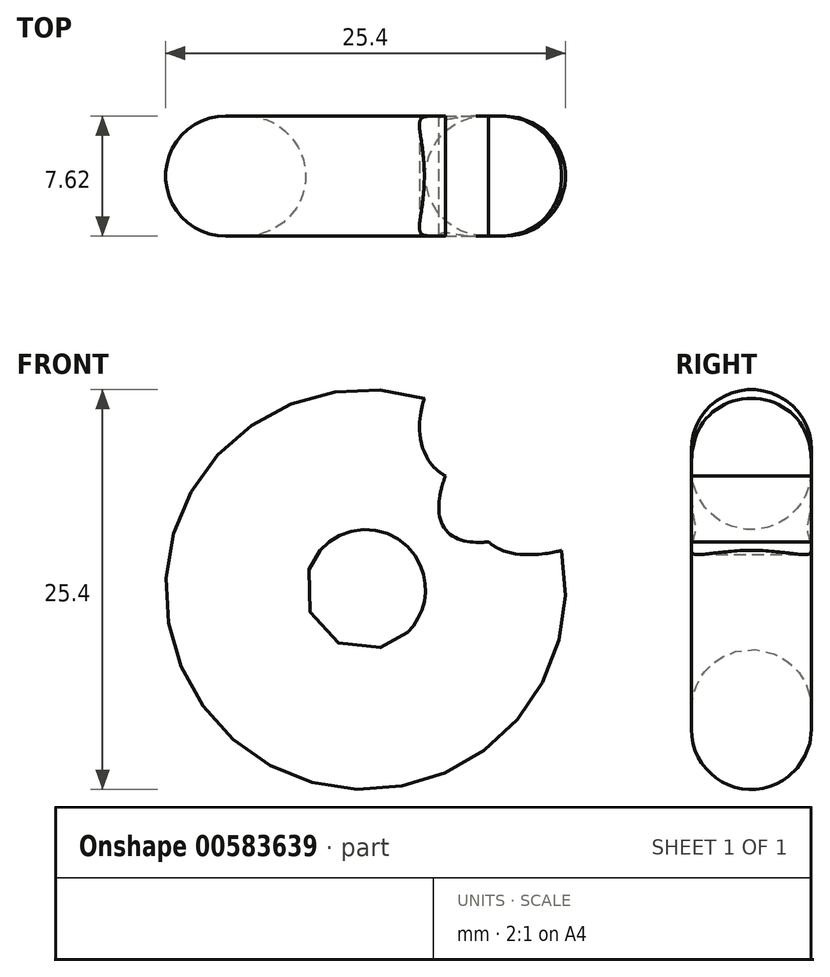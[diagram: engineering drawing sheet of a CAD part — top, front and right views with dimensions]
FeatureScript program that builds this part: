
annotation { "Feature Type Name" : "Feature", "Feature Type Description" : "" }
export const myFeature = defineFeature(function(context is Context, id is Id, definition is map)
    precondition{}
    {
        {
            var Q0;
            Q0=qCreatedBy(makeId("Front.planeOp"),FACE);
            var sketch = newSketch(context, id + "F0", { "sketchPlane" : qUnion([Q0])});
            skArc(sketch, "E0", {"start": v(0, 12.7) * mm, "mid": v(-8.98, -8.98) * mm, "end": v(12.7, 0) * mm});
            skArc(sketch, "E1", {"start": v(0, 3.81) * mm, "mid": v(-2.7, -2.7) * mm, "end": v(3.81, 0) * mm});
            skArc(sketch, "E2", {"start": v(0, 12.7) * mm, "mid": v(8.98, 8.98) * mm, "end": v(12.7, 0) * mm});
            skArc(sketch, "E3", {"start": v(0, 3.81) * mm, "mid": v(2.7, 2.7) * mm, "end": v(3.81, 0) * mm});
            skPoint(sketch, "E4", {"position": v(8.98, 8.98) * mm});
            skEllipse(sketch, "E5", {"center": v(8.98, 12.27) * mm, "majorRadius": 6.46 * mm, "minorRadius": 4.47 * mm, "majorAxis": v(-0.7, -0.7)});
            skEllipse(sketch, "E6", {"center": v(13.9, 7.03) * mm, "majorRadius": 7.35 * mm, "minorRadius": 3.72 * mm, "majorAxis": v(-0.88, -0.48)});
            skEllipticalArc(sketch, "E7", {});
            const initialGuessF0  = {"E7": [0.017075618728995323, 0.013890886679291725, -0.762498905092994, -0.6469895051173437, 0.015677614206353045, 0.0052293633850373335, 4.771161160451003, 1.5778972296702722]};
            skSetInitialGuess(sketch, initialGuessF0);
            skSolve(sketch);
        }
        {
            var Q0;
            Q0=makeQuery(id+"F0.imprint","IMPRINT",FACE,{"disambiguationData":[TD([[makeQuery(id+"F0.imprint","IMPRINT",EDGE,{"derivedFrom":sQuery(id+"F0.wireOp",EDGE,"E0")}),1.0]])]});
            extrude(context, id + "F1", {"entities" : qUnion([Q0]), "depth" : 7.62 * mm, "offsetDistance" : 25.4 * mm});
        }
        {
            var Q0;
            Q0=makeQuery(id+"F1.opExtrude","CAP_EDGE",EDGE,{"disambiguationData":[OSD([sQuery(id+"F0.wireOp",EDGE,"E0"),sQuery(id+"F0.wireOp",EDGE,"E2")])],"isStart":true});
            var Q1;
            Q1=makeQuery(id+"F1.opExtrude","CAP_EDGE",EDGE,{"disambiguationData":[OSD([sQuery(id+"F0.wireOp",EDGE,"E0"),sQuery(id+"F0.wireOp",EDGE,"E2")])],"isStart":false});
            fillet(context, id + "F2", {"entities" : qUnion([Q0, Q1]), "radius" : 3.8 * mm, "tangentPropagation" : true, "allowEdgeOverflow" : false});
        }
        {
            var Q0;
            Q0=makeQuery(id+"F1.opExtrude","CAP_EDGE",EDGE,{"disambiguationData":[OSD([sQuery(id+"F0.wireOp",EDGE,"E1"),sQuery(id+"F0.wireOp",EDGE,"E3")])],"isStart":true});
            var Q1;
            Q1=makeQuery(id+"F1.opExtrude","CAP_EDGE",EDGE,{"disambiguationData":[OSD([sQuery(id+"F0.wireOp",EDGE,"E1"),sQuery(id+"F0.wireOp",EDGE,"E3")])],"isStart":false});
            fillet(context, id + "F3", {"entities" : qUnion([Q0, Q1]), "radius" : 3.8 * mm, "tangentPropagation" : true, "allowEdgeOverflow" : false});
        }
    });
